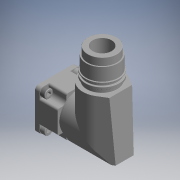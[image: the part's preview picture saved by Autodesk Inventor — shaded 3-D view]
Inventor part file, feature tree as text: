
AUTODESK INVENTOR PART (.ipt)
format: ipt  version: 2017.3 (Build 213256000, 256)  size: 345,088 bytes
history: native  units: mm (DEFAULTED — no unit token found)
features: sketch x16, extrude x10, other x7, revolve x6
ambient origin geometry x8: Origin, YZ Plane, XZ Plane, XY Plane, X Axis, Y Axis, Z Axis, Center Point
bodies: Solid1 (feature_tree)
feature tree (39):
  extrude  "Extrusion1"  Depth=9.5mm TaperAngle=0.0deg
  extrude  "Extrusion2"  Depth=24.18mm TaperAngle=0.0deg
  revolve  "Revolution1"  [1 undecoded]
  extrude  "Extrusion3"  Depth=30.25mm TaperAngle=0.0deg
  revolve  "Revolution2"  Angle=360.0deg
  extrude  "Extrusion4"  TaperAngle=360.0deg  [1 undecoded]
  extrude  "Extrusion5"  Depth=2.0mm TaperAngle=0.0deg
  extrude  "Extrusion6"  Depth=2.0mm TaperAngle=0.0deg
  revolve  "Revolution3"  [1 undecoded]
  revolve  "Revolution4"  [1 undecoded]
  revolve  "Revolution5"  [1 undecoded]
  revolve  "Revolution6"  [1 undecoded]
  extrude  "Extrusion7"  [1 undecoded]
  extrude  "Extrusion8"  [1 undecoded]
  extrude  "Extrusion9"  [1 undecoded]
  extrude  "Extrusion10"  [1 undecoded]
  other  "geh_XY"
  other  "geh_YZ"
  other  "geh_ZX"
  other  "geh_X"
  other  "geh_Y"
  other  "geh_Z"
  other  "geh_Center"
  sketch  "Sketch_7"  dims[d0=12.0mm d1=0.0mm d2=9.5mm d3=0.0mm]
  sketch  "Sketch_8"  dims[d4=360.0deg d5=24.18mm d6=0.0mm]
  sketch  "Sketch_9"  dims[d7=360.0deg d8=20.25mm d9=0.0mm]
  sketch  "Sketch_10"  dims[d10=30.6878mm d11=0.0mm d12=30.25mm d13=0.0mm]
  sketch  "Sketch_11"  dims[d14=360.0deg d15=360.0deg]
  sketch  "Sketch_13"  dims[d18=2.0mm d19=0.0mm d20=2.0mm d21=0.0mm]
  sketch  "Sketch_12"  dims[d16=360.0deg d17=360.0deg]
  sketch  "Sketch_14"  dims[d22=2.0mm d23=0.0mm d24=2.0mm d25=0.0mm]
  sketch  "Sketch_31"  dims[d26=0.0mm]
  sketch  "Sketch_32"
  sketch  "Sketch_33"
  sketch  "Sketch_34"
  sketch  "Sketch_35"
  sketch  "Sketch_36"
  sketch  "Sketch_37"
  sketch  "Sketch_38"
note: 10 required parameter values undecoded (feature->parameter linkage not recoverable at this tier; creation-order binding heuristic only, values carry confidence <= 0.55)